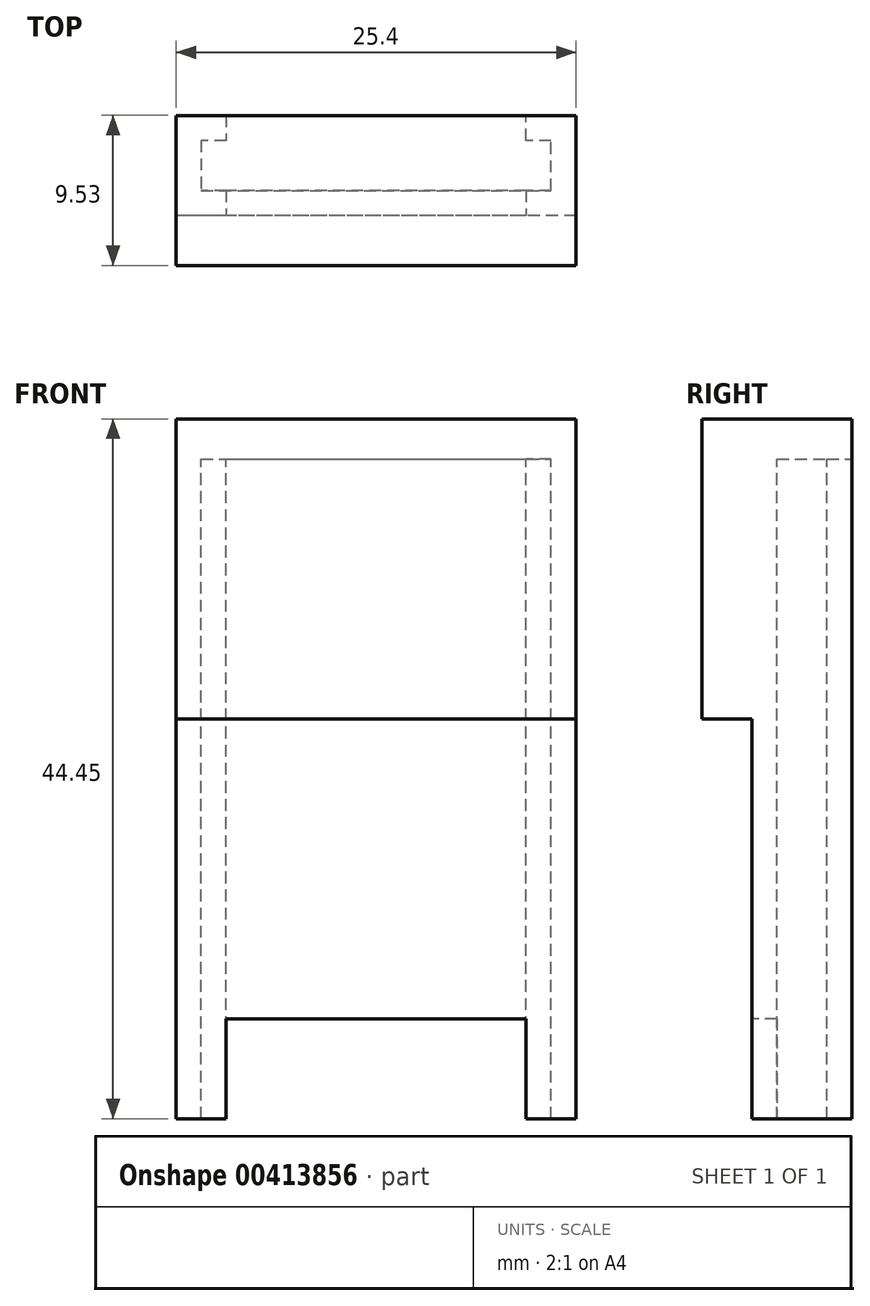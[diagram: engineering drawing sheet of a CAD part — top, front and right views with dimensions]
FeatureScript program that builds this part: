
annotation { "Feature Type Name" : "Feature", "Feature Type Description" : "" }
export const myFeature = defineFeature(function(context is Context, id is Id, definition is map)
    precondition{}
    {
        {
            var Q0;
            Q0=qCreatedBy(makeId("Top.planeOp"),FACE);
            var sketch = newSketch(context, id + "F0", { "sketchPlane" : qUnion([Q0])});
            skLineSegment(sketch, "E0", {"start": v(0, 0) * mm, "end": v(25.4, 0) * mm});
            skLineSegment(sketch, "E1", {"start": v(25.4, 0) * mm, "end": v(25.4, 3.18) * mm});
            skLineSegment(sketch, "E2", {"start": v(25.4, 3.18) * mm, "end": v(0, 3.18) * mm});
            skLineSegment(sketch, "E3", {"start": v(0, 3.18) * mm, "end": v(0, 0) * mm});
            skSolve(sketch);
        }
        {
            var Q0;
            Q0 = qSketchRegion(id + "F0", true);
            extrude(context, id + "F1", {"entities" : qUnion([Q0]), "depth" : 19.05 * mm});
        }
        {
            var Q0;
            Q0=makeQuery(id+"F1.opExtrude","CAP_FACE",FACE,{"disambiguationData":[OSD([sQuery(id+"F0.wireOp",EDGE,"E0"),sQuery(id+"F0.wireOp",EDGE,"E1"),sQuery(id+"F0.wireOp",EDGE,"E2"),sQuery(id+"F0.wireOp",EDGE,"E3")])],"isStart":true});
            var sketch = newSketch(context, id + "F2", { "sketchPlane" : qUnion([Q0])});
            skLineSegment(sketch, "E4", {"start": v(25.4, -3.18) * mm, "end": v(25.4, -9.53) * mm});
            skLineSegment(sketch, "E5", {"start": v(25.4, -9.53) * mm, "end": v(23.81, -9.53) * mm});
            skLineSegment(sketch, "E6", {"start": v(23.81, -9.53) * mm, "end": v(22.23, -9.53) * mm});
            skLineSegment(sketch, "E7", {"start": v(22.23, -9.53) * mm, "end": v(22.23, -7.94) * mm});
            skLineSegment(sketch, "E8", {"start": v(22.23, -7.94) * mm, "end": v(23.81, -7.94) * mm});
            skLineSegment(sketch, "E9", {"start": v(23.81, -7.94) * mm, "end": v(23.81, -4.76) * mm});
            skLineSegment(sketch, "E10.MirrorCS", {"start": v(3.17, -7.94) * mm, "end": v(1.59, -7.94) * mm});
            skLineSegment(sketch, "E11.MirrorCS", {"start": v(3.17, -9.53) * mm, "end": v(3.17, -7.94) * mm});
            skLineSegment(sketch, "E12.MirrorCS", {"start": v(1.59, -9.53) * mm, "end": v(3.17, -9.53) * mm});
            skLineSegment(sketch, "E13.MirrorCS", {"start": v(0, -9.53) * mm, "end": v(1.59, -9.53) * mm});
            skLineSegment(sketch, "E14.MirrorCS", {"start": v(1.59, -7.94) * mm, "end": v(1.59, -4.76) * mm});
            skLineSegment(sketch, "E15.MirrorCS", {"start": v(0, -3.18) * mm, "end": v(0, -9.53) * mm});
            skLineSegment(sketch, "E16", {"start": v(23.81, -4.76) * mm, "end": v(1.59, -4.76) * mm});
            skLineSegment(sketch, "E17", {"start": v(25.4, -3.18) * mm, "end": v(0, -3.18) * mm});
            skSolve(sketch);
        }
        {
            var Q0;
            Q0 = qSketchRegion(id + "F2", true);
            extrude(context, id + "F3", {"entities" : qUnion([Q0]), "operationType" : NewBodyOperationType.ADD, "depth" : 25.4 * mm, "hasSecondDirection" : true, "secondDirectionOppositeDirection" : true, "secondDirectionDepth" : 19.05 * mm});
        }
        {
            var Q0;
            Q0=makeQuery(id+"F3.boolean.opBoolean","MERGE",FACE,{"derivedFrom":[makeQuery(id+"F1.opExtrude","CAP_FACE",FACE,{"disambiguationData":[OSD([sQuery(id+"F0.wireOp",EDGE,"E0"),sQuery(id+"F0.wireOp",EDGE,"E1"),sQuery(id+"F0.wireOp",EDGE,"E2"),sQuery(id+"F0.wireOp",EDGE,"E3")])],"isStart":false}),makeQuery(id+"F3.opExtrude","CAP_FACE",FACE,{"disambiguationData":[OSD([sQuery(id+"F2.wireOp",EDGE,"E4"),sQuery(id+"F2.wireOp",EDGE,"E5"),sQuery(id+"F2.wireOp",EDGE,"E6"),sQuery(id+"F2.wireOp",EDGE,"E7"),sQuery(id+"F2.wireOp",EDGE,"E8"),sQuery(id+"F2.wireOp",EDGE,"E9"),sQuery(id+"F2.wireOp",EDGE,"E10.MirrorCS"),sQuery(id+"F2.wireOp",EDGE,"E11.MirrorCS"),sQuery(id+"F2.wireOp",EDGE,"E12.MirrorCS"),sQuery(id+"F2.wireOp",EDGE,"E13.MirrorCS"),sQuery(id+"F2.wireOp",EDGE,"E14.MirrorCS"),sQuery(id+"F2.wireOp",EDGE,"E15.MirrorCS"),sQuery(id+"F2.wireOp",EDGE,"E16"),sQuery(id+"F2.wireOp",EDGE,"E17")])],"isStart":true})]});
            var sketch = newSketch(context, id + "F4", { "sketchPlane" : qUnion([Q0])});
            skLineSegment(sketch, "E18.bottom", {"start": v(0, 0) * mm, "end": v(25.4, 0) * mm});
            skLineSegment(sketch, "E18.top", {"start": v(0, 9.53) * mm, "end": v(25.4, 9.53) * mm});
            skLineSegment(sketch, "E18.left", {"start": v(0, 0) * mm, "end": v(0, 9.53) * mm});
            skLineSegment(sketch, "E18.right", {"start": v(25.4, 0) * mm, "end": v(25.4, 9.53) * mm});
            skSolve(sketch);
        }
        {
            var Q0;
            Q0 = qSketchRegion(id + "F4", true);
            extrude(context, id + "F5", {"entities" : qUnion([Q0]), "operationType" : NewBodyOperationType.ADD, "oppositeDirection" : true, "depth" : 2.54 * mm});
        }
        {
            var Q0;
            Q0=makeQuery(id+"F3.opExtrude","CAP_FACE",FACE,{"disambiguationData":[OSD([sQuery(id+"F2.wireOp",EDGE,"E4"),sQuery(id+"F2.wireOp",EDGE,"E5"),sQuery(id+"F2.wireOp",EDGE,"E6"),sQuery(id+"F2.wireOp",EDGE,"E7"),sQuery(id+"F2.wireOp",EDGE,"E8"),sQuery(id+"F2.wireOp",EDGE,"E9"),sQuery(id+"F2.wireOp",EDGE,"E10.MirrorCS"),sQuery(id+"F2.wireOp",EDGE,"E11.MirrorCS"),sQuery(id+"F2.wireOp",EDGE,"E12.MirrorCS"),sQuery(id+"F2.wireOp",EDGE,"E13.MirrorCS"),sQuery(id+"F2.wireOp",EDGE,"E14.MirrorCS"),sQuery(id+"F2.wireOp",EDGE,"E15.MirrorCS"),sQuery(id+"F2.wireOp",EDGE,"E16"),sQuery(id+"F2.wireOp",EDGE,"E17")])],"isStart":false});
            var sketch = newSketch(context, id + "F6", { "sketchPlane" : qUnion([Q0])});
            skLineSegment(sketch, "E19", {"start": v(22.23, -3.18) * mm, "end": v(3.17, -3.18) * mm});
            skLineSegment(sketch, "E20", {"start": v(3.17, -4.76) * mm, "end": v(22.23, -4.76) * mm});
            skLineSegment(sketch, "E21", {"start": v(22.23, -4.76) * mm, "end": v(22.23, -3.18) * mm});
            skLineSegment(sketch, "E22", {"start": v(3.17, -4.76) * mm, "end": v(3.17, -3.18) * mm});
            skPoint(sketch, "E23.orphan", {"position": v(1.59, -3.18) * mm});
            skSolve(sketch);
        }
        {
            var Q0;
            Q0 = qSketchRegion(id + "F6", true);
            extrude(context, id + "F7", {"entities" : qUnion([Q0]), "operationType" : NewBodyOperationType.REMOVE, "oppositeDirection" : true, "depth" : 6.35 * mm});
        }
    });
